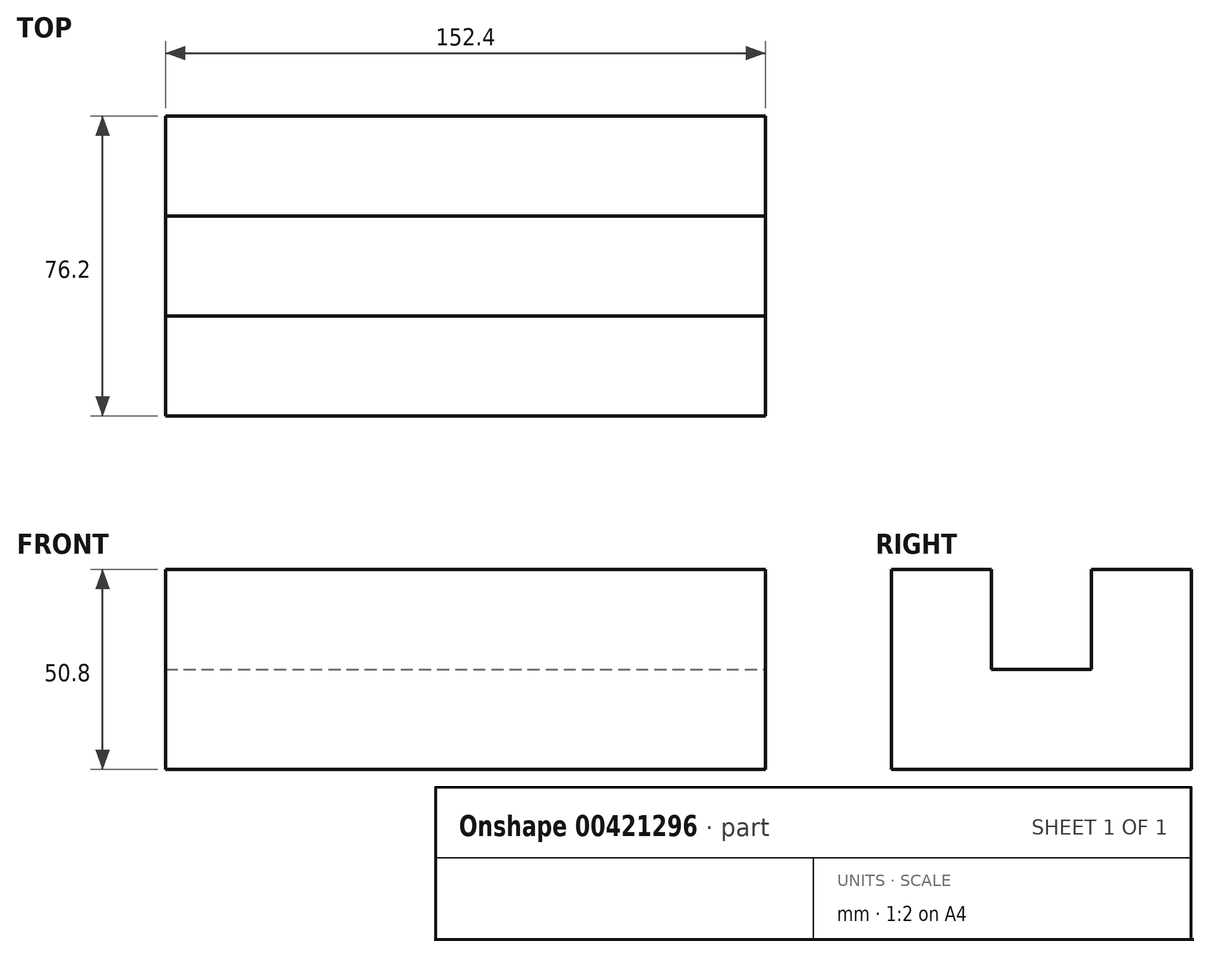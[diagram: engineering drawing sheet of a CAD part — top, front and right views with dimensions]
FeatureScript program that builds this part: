
annotation { "Feature Type Name" : "Feature", "Feature Type Description" : "" }
export const myFeature = defineFeature(function(context is Context, id is Id, definition is map)
    precondition{}
    {
        {
            var Q0;
            Q0=qCreatedBy(makeId("Right.planeOp"),FACE);
            var sketch = newSketch(context, id + "F0", { "sketchPlane" : qUnion([Q0])});
            skLineSegment(sketch, "E0", {"start": v(0, 0) * mm, "end": v(76.2, 0) * mm});
            skLineSegment(sketch, "E1", {"start": v(76.2, 0) * mm, "end": v(76.2, 50.8) * mm});
            skLineSegment(sketch, "E2", {"start": v(0, 0) * mm, "end": v(0, 50.8) * mm});
            skLineSegment(sketch, "E3", {"start": v(0, 50.8) * mm, "end": v(25.4, 50.8) * mm});
            skLineSegment(sketch, "E4", {"start": v(76.2, 50.8) * mm, "end": v(50.8, 50.8) * mm});
            skLineSegment(sketch, "E5", {"start": v(25.4, 50.8) * mm, "end": v(25.4, 25.4) * mm});
            skLineSegment(sketch, "E6", {"start": v(50.8, 50.8) * mm, "end": v(50.8, 25.4) * mm});
            skLineSegment(sketch, "E7", {"start": v(25.4, 25.4) * mm, "end": v(50.8, 25.4) * mm});
            skSolve(sketch);
        }
        {
            var Q0;
            Q0=makeQuery(id+"F0.imprint","IMPRINT",FACE,{"disambiguationData":[TD([[makeQuery(id+"F0.imprint","IMPRINT",EDGE,{"derivedFrom":sQuery(id+"F0.wireOp",EDGE,"E0")}),1.0]])]});
            extrude(context, id + "F1", {"entities" : qUnion([Q0]), "oppositeDirection" : true, "depth" : 152.4 * mm});
        }
    });
